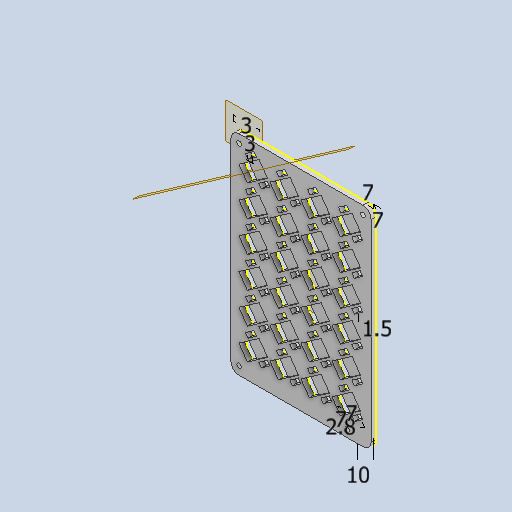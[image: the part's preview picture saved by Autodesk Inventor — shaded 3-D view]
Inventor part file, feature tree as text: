
AUTODESK INVENTOR PART (.ipt)
format: ipt  version: 2022 (Build 260153000, 153)  size: 434,688 bytes
history: native  units: mm
features: sketch x5, plane x4, extrude x4, reference x3, other x2, mirror x1, pattern_linear x1, projected_geometry x1
ambient origin geometry x8: Origin, YZ Plane, XZ Plane, XY Plane, X Axis, Y Axis, Z Axis, Center Point
bodies: Volumenkörper1 (feature_tree)
feature tree (21):
  plane  "Arbeitsebene4"
  sketch  "Skizze1"  dims[d0=1.5mm d1=3.0mm]
  plane  "Arbeitsebene2"
  plane  "Arbeitsebene6"
  extrude  "Extrusion2"  Depth=3.0mm
  extrude  "Extrusion3"  Depth=3.0mm
  extrude  "Extrusion4"  Depth=7.0mm
  extrude  "Extrusion5"  Depth=10.0mm
  plane  "Arbeitsebene7"
  mirror  "Spiegeln1"
  pattern_linear  "Rechteckige Anordnung3"  Spacing1=3.0mm  [1 undecoded]
  sketch  "Skizze2"  dims[d2=3.0mm d5=7.0mm]
  projected_geometry  "Projizierte Kontur1"
  sketch  "Skizze3"  dims[d6=7.0mm d7=7.0mm]
  sketch  "Skizze4"  dims[d8=7.0mm d9=10.0mm]
  sketch  "Skizze5"  dims[d10=2.8mm d11=3.0mm d12=0.0mm d15=21.816616mm d19=9.0mm d20=6.0mm d21=55.0mm d22=0.0mm d35=9.0mm d36=1.0mm d37=0.0mm d40=2.5mm d41=2.7mm d42=0.3mm d43=0.0mm d44=0.0mm d45=60.0mm d47=18.9mm d48=40.0mm d50=18.9mm d51=0.3mm d52=0.3mm]
  reference  "Referenz5"
  reference  "Referenz6"
  reference  "Referenz7"
  other  "Omniscope_new_v0.iam"
  other  "Omniscope_Camera_fix:1"
note: 1 required parameter value undecoded (feature->parameter linkage not recoverable at this tier; creation-order binding heuristic only, values carry confidence <= 0.55)
